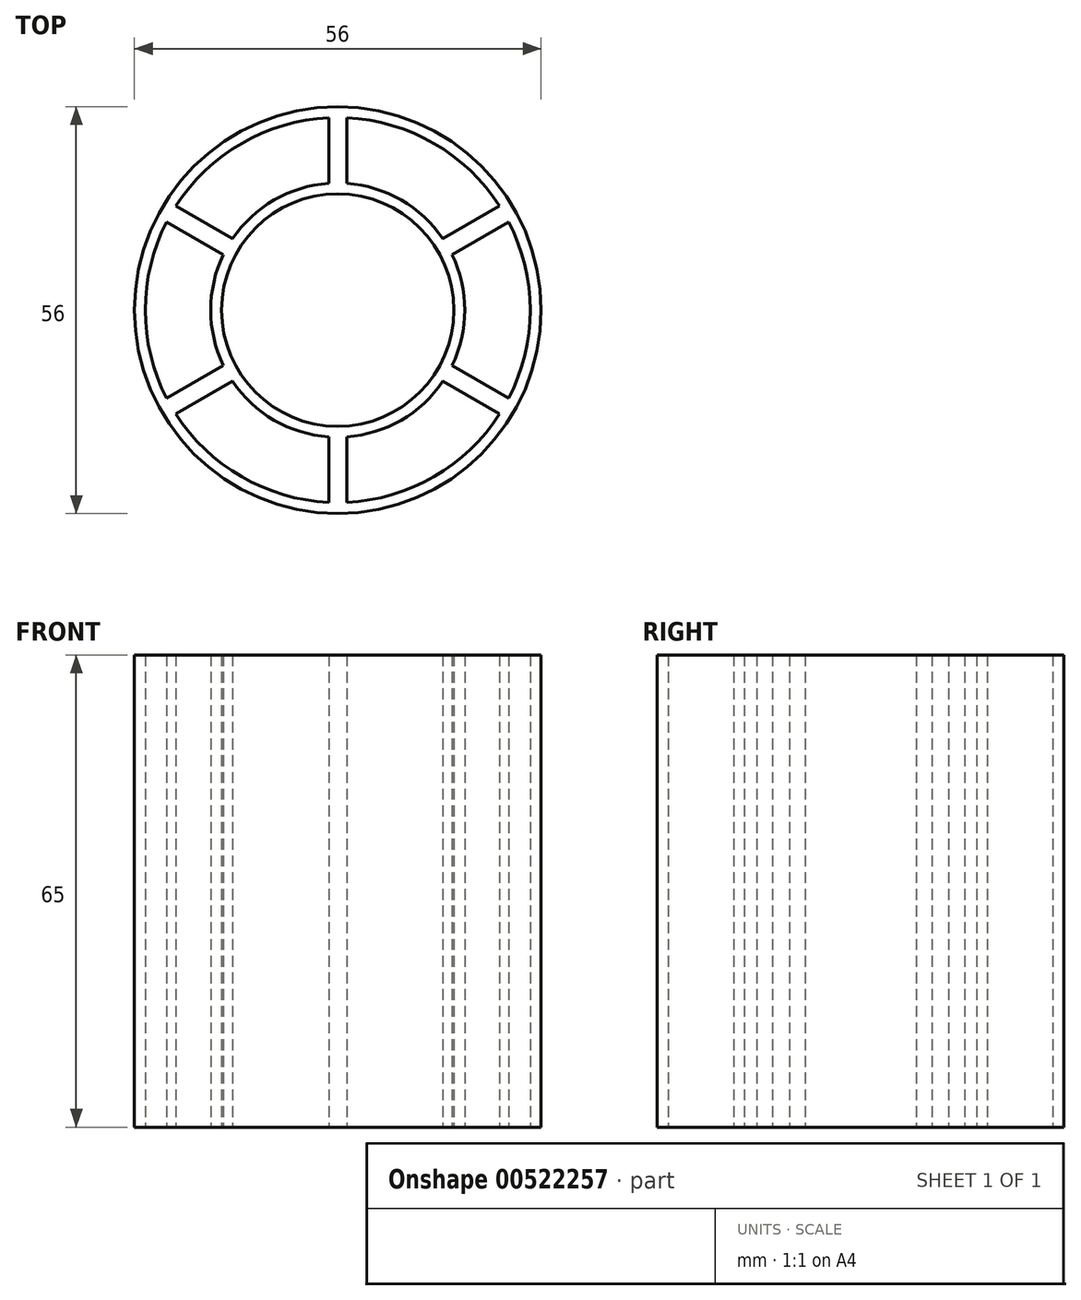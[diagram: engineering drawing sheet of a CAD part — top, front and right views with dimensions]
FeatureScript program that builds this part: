
annotation { "Feature Type Name" : "Feature", "Feature Type Description" : "" }
export const myFeature = defineFeature(function(context is Context, id is Id, definition is map)
    precondition{}
    {
        {
            var Q0;
            Q0=qCreatedBy(makeId("Top.planeOp"),FACE);
            var sketch = newSketch(context, id + "F0", { "sketchPlane" : qUnion([Q0])});
            skCircle(sketch, "E0", {"center": v(0, 0) * mm, "radius": 17.5 * mm});
            skCircle(sketch, "E1", {"center": v(0, 0) * mm, "radius": 16 * mm});
            skCircle(sketch, "E2", {"center": v(0, 0) * mm, "radius": 26.5 * mm});
            skCircle(sketch, "E3", {"center": v(0, 0) * mm, "radius": 28 * mm});
            skLineSegment(sketch, "E4", {"start": v(0, 17.5) * mm, "end": v(0, 26.5) * mm, "construction": true});
            skLineSegment(sketch, "E5", {"start": v(-1.25, 26.47) * mm, "end": v(-1.25, 17.46) * mm});
            skLineSegment(sketch, "E6", {"start": v(1.25, 26.47) * mm, "end": v(1.25, 17.46) * mm});
            skLineSegment(sketch, "E7.1.0", {"start": v(-23.55, 12.15) * mm, "end": v(-15.74, 7.65) * mm});
            skLineSegment(sketch, "E7.1.1", {"start": v(-22.3, 14.32) * mm, "end": v(-14.5, 9.81) * mm});
            skLineSegment(sketch, "E7.2.0", {"start": v(-22.3, -14.32) * mm, "end": v(-14.5, -9.81) * mm});
            skLineSegment(sketch, "E7.2.1", {"start": v(-23.55, -12.15) * mm, "end": v(-15.74, -7.65) * mm});
            skLineSegment(sketch, "E7.3.0", {"start": v(1.25, -26.47) * mm, "end": v(1.25, -17.46) * mm});
            skLineSegment(sketch, "E7.3.1", {"start": v(-1.25, -26.47) * mm, "end": v(-1.25, -17.46) * mm});
            skLineSegment(sketch, "E7.4.0", {"start": v(23.55, -12.15) * mm, "end": v(15.74, -7.65) * mm});
            skLineSegment(sketch, "E7.4.1", {"start": v(22.3, -14.32) * mm, "end": v(14.5, -9.81) * mm});
            skLineSegment(sketch, "E7.5.0", {"start": v(22.3, 14.32) * mm, "end": v(14.5, 9.81) * mm});
            skLineSegment(sketch, "E7.5.1", {"start": v(23.55, 12.15) * mm, "end": v(15.74, 7.65) * mm});
            skSolve(sketch);
        }
        {
            var Q0;
            Q0=makeQuery(id+"F0.imprint","IMPRINT",FACE,{"disambiguationData":[TD([[makeQuery(id+"F0.imprint","IMPRINT",EDGE,{"derivedFrom":sQuery(id+"F0.wireOp",EDGE,"E1")}),-1.0]])]});
            var Q1;
            Q1=makeQuery(id+"F0.imprint","IMPRINT",FACE,{"disambiguationData":[TD([[makeQuery(id+"F0.imprint","IMPRINT",EDGE,{"derivedFrom":sQuery(id+"F0.wireOp",EDGE,"E3")}),1.0]])]});
            extrude(context, id + "F1", {"entities" : qUnion([Q0, Q1]), "depth" : 65 * mm, "offsetDistance" : 25 * mm, "symmetric" : true});
        }
        {
            var Q0;
            {var subQ0=sQuery(id+"F0.wireOp",EDGE,"E7.1.0");Q0=makeQuery(id+"F0.imprint","IMPRINT",FACE,{"disambiguationData":[TD([[makeQuery(id+"F0.imprint","IMPRINT",EDGE,{"derivedFrom":subQ0}),1.0]])]});}
            var Q1;
            {var subQ0=sQuery(id+"F0.wireOp",EDGE,"E5");Q1=makeQuery(id+"F0.imprint","IMPRINT",FACE,{"disambiguationData":[TD([[makeQuery(id+"F0.imprint","IMPRINT",EDGE,{"derivedFrom":subQ0}),1.0]])]});}
            var Q2;
            {var subQ0=sQuery(id+"F0.wireOp",EDGE,"E7.5.0");Q2=makeQuery(id+"F0.imprint","IMPRINT",FACE,{"disambiguationData":[TD([[makeQuery(id+"F0.imprint","IMPRINT",EDGE,{"derivedFrom":subQ0}),1.0]])]});}
            var Q3;
            {var subQ0=sQuery(id+"F0.wireOp",EDGE,"E7.4.0");Q3=makeQuery(id+"F0.imprint","IMPRINT",FACE,{"disambiguationData":[TD([[makeQuery(id+"F0.imprint","IMPRINT",EDGE,{"derivedFrom":subQ0}),1.0]])]});}
            var Q4;
            {var subQ0=sQuery(id+"F0.wireOp",EDGE,"E7.3.0");Q4=makeQuery(id+"F0.imprint","IMPRINT",FACE,{"disambiguationData":[TD([[makeQuery(id+"F0.imprint","IMPRINT",EDGE,{"derivedFrom":subQ0}),1.0]])]});}
            var Q5;
            {var subQ0=sQuery(id+"F0.wireOp",EDGE,"E7.2.0");Q5=makeQuery(id+"F0.imprint","IMPRINT",FACE,{"disambiguationData":[TD([[makeQuery(id+"F0.imprint","IMPRINT",EDGE,{"derivedFrom":subQ0}),1.0]])]});}
            extrude(context, id + "F2", {"entities" : qUnion([Q0, Q1, Q2, Q3, Q4, Q5]), "operationType" : NewBodyOperationType.ADD, "depth" : 65 * mm, "offsetDistance" : 25 * mm, "symmetric" : true});
        }
    });
